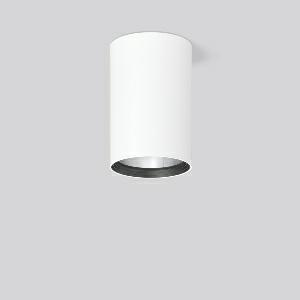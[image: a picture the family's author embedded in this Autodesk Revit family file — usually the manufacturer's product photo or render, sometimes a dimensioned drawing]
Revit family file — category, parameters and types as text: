
# Revit family: heledon_maxi_a_931218_002_3_76_1967
name_source: partatom
category: Lighting Fixtures
units: mm (PartAtom-declared; Revit-internal decimal feet)

## family parameters
Cut with Voids When Loaded = No
Host = Face
Light Source = No
Part Type = Normal
Room Calculation Point = No
Round Connector Dimension = Use Diameter
Shared = No

## types (1)
- HELEDON maxi A (1 x LED Modul 935, 3400 lm, 3500)
    Apparent Load = 25 VA
    Approval mark = CE
    CIE Flux Codes = 100 100 100 100 100
    Color Rendering = 92
    Color Temperature = 3500
    Default Elevation = 1800 mm
    Description = Series: HELEDON maxi
Cylindrical surface-mounted downlight. Housing: die-cast aluminium, powder-coated. Internal ceiling frame polycarbonate with bayonet mounting. Black plastic ring and recessed LED to prevent glare from the side. Optical assembly with reflector made of MIRO-Silver with 98% total light reflection for outstanding efficiency - can be changed without tools. Best colour rendering index Ra>90. Suitable for Ceiling mounting. Easy installation with a separate ceiling frame with bayonet mounting and plug connection. Driver integrated. Connected via plug-in connector. High quality converter without flickering and stroboscopic effect. The following accessories can be mounted without use of tools: interchangeable lenses, decorative glasses, honeycomb louvre, clear and frosted diffusers, white interchangeable plastic ring. 
Colour: traffic white, matt (RAL 9016)
Diameter: 123 mm
Height: 183 mm
Lamp: LED
Socket: without socket
Colour temperature: 3500K
Colour rendering index (CRI): 92
System power: 25 W
Rated luminous flux: 3400 lm
Luminous efficiency: 136 lm/W
Control gear: Converter, dimmable, DALI
Protection class: I
Type of protection: IP 20
    Height = 183 mm
    Lamp = 1 x LED Modul 935
    Lamp Light Flux = 3400 lm
    Lamp count = 1
    Length = 123 mm
    Lifetime = 50000 h
    Luminous efficacy = 136 lm/W
    Manufacturer = RZB
    ModVariant = No
    Model = 931218.002.3.76
    Mounting Place = Ceiling
    Mounting Type = Surface mounted
    Number of Poles = 1
    OnlyDefault = Yes
    Power Factor = 1
    Product Name = HELEDON maxi A
    Product group = Surface mounted downlights
    ProductGroupID = 302
    Protection Class = Protection class I
    Protection Degree = IP 20
    RLX_Detail_Level = 1
    RLX_Emergency_Light_Flux = 0 lm
    RLX_Emergency_Type = 0
    RLX_Emergency_Type_DB = No
    RlxData = <blob elided: 95653 chars, md5=2ccdeddb>
    Socket = socket
    Standby Power = 0 W
    System Light Flux = 3400 lm
    System Power = 25 W
    Type Comments = Product without accessories
    Type Image = 931192.002.jpg
    URL = http://relux.com
    VarID = ---
    Voltage = 230 V
    Voltage Range = 220-240 V
    Weight = 0.00 kg
    Width = 0 mm  [stored 0 ft]

note: [stored X ft] marks values corroborated as IEEE doubles in the binary element streams (Revit-internal decimal feet)

## geometry (parser evidence)
native form markers: Blend x4, Sweep x11
no freeform markers — native parametric forms only
